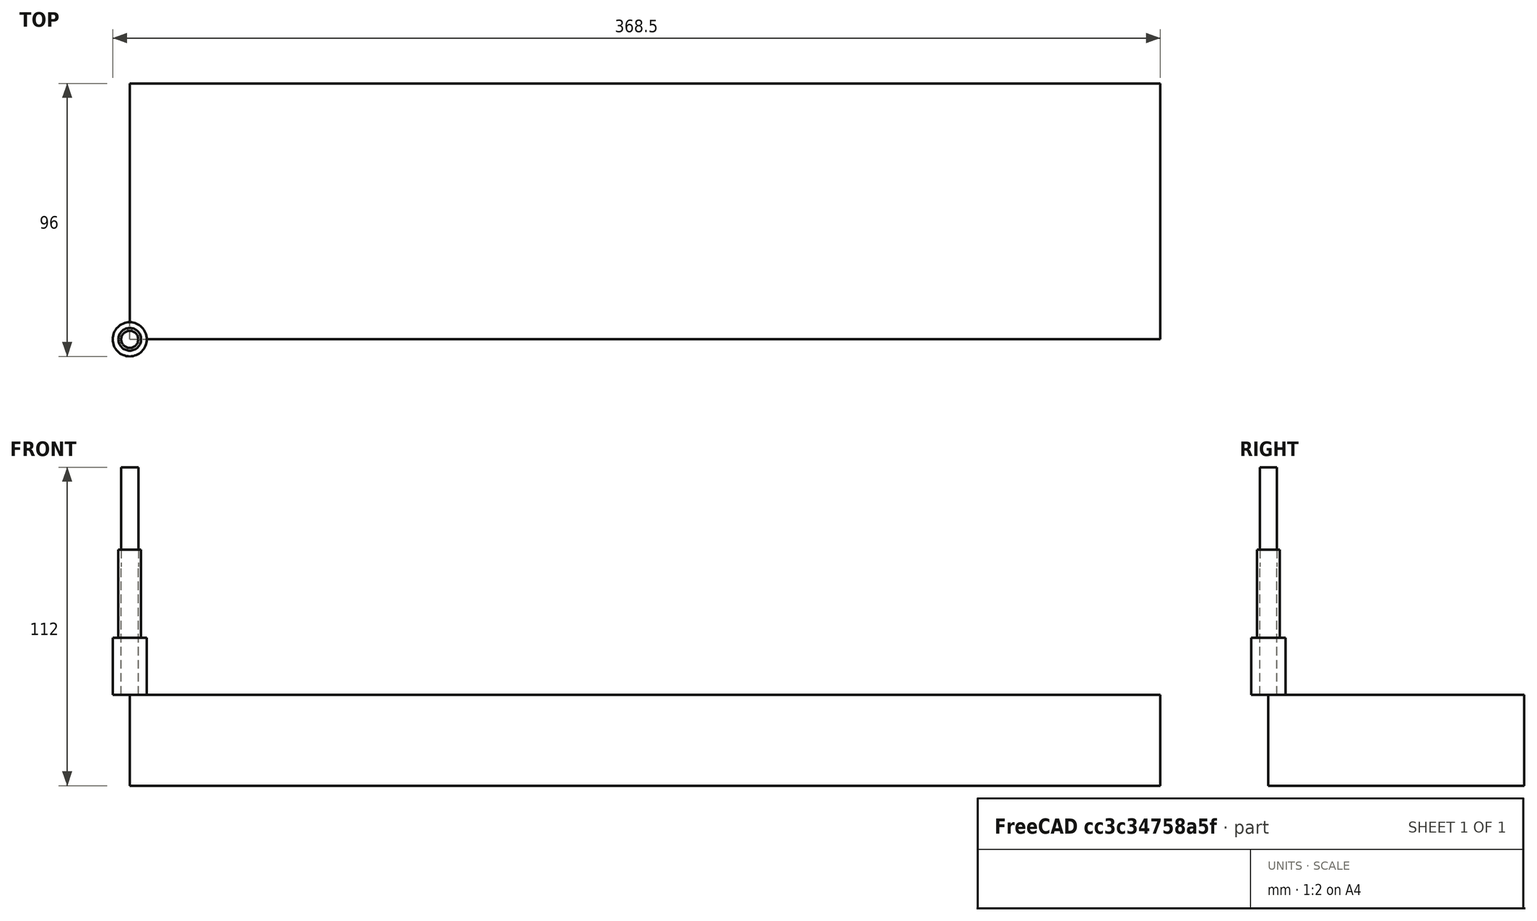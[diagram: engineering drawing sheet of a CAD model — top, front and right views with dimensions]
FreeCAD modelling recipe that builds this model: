
FCSTD DOCUMENT  (FreeCAD 0.22R34789 (Git))
Label: fence_side_reversal
License: All rights reserved
LicenseURL: http://en.wikipedia.org/wiki/All_rights_reserved
objects: Path::FeaturePython×7, Part::FeaturePython×5, App::DocumentObjectGroup×3, App::FeaturePython×1
note: 8 computed .brp shape members not serialized (recipe doc carries the construction recipe); baked Part::Feature solids carry a one-line shape summary decoded from their .brp

FEATURE [Part::FeaturePython] b_drill_press_table_001_  label="drill_press_table_fence_face_r_001"  # a2plus imported part (geometry in sourceFile) (typed FeaturePython)
  Placement = pos=(0,0,0) rot=(1,0,0;1.5708rad)
  a2p_Version = 0.4.61
  fixedPosition = true
  objectType = a2pPart
  sourceFile = ./../drill_press_table.FCStd
  sourcePart = fence_face_r
  subassemblyImport = false
  timeLastImport = 1.69948e+09
  updateColors = true
FEATURE [App::FeaturePython] SetupSheet  # Path/CAM operation (typed FeaturePython)
  ClearanceHeightExpression = OpStockZMax+SetupSheet.ClearanceHeightOffset
  ClearanceHeightOffset = 5
  CoolantMode = 0
  CoolantModes = None | Flood | Mist
  FinalDepthExpression = OpFinalDepth
  HorizRapid = 0
  SafeHeightExpression = OpStockZMax+SetupSheet.SafeHeightOffset
  SafeHeightOffset = 3
  StartDepthExpression = OpStartDepth
  StepDownExpression = OpToolDiameter
  VertRapid = 0
FEATURE [Part::FeaturePython] Clone  label="Model-drill_press_table_fence_face_r_001"  # Draft clone (typed FeaturePython)
  AttacherType = Attacher::AttachEngine3D
  Fuse = false
  Objects = -> [b_drill_press_table_001_]
  PathResource = Model
  Placement = pos=(-7.5,116,-306) rot=(1,0,0;1.5708rad)
  Scale = (1,1,1)
FEATURE [App::DocumentObjectGroup] Model
  Group = -> [Clone]
FEATURE [Part::FeaturePython] Stock  # WARN: FeaturePython — macro-defined, semantics opaque (R4)
  Base = -> Model
  ExtXneg = 15
  ExtXpos = 10
  ExtYneg = 15
  ExtYpos = 10
  ExtZneg = 0
  ExtZpos = 0
  Placement = pos=(15,15,-32) rot=(0,0,1;0rad)
  StockType = FromBase
FEATURE [Part::FeaturePython] ToolBit001  label="6 mm endmill, D=6, H=45, L=80, S=6"  # Path/CAM toolbit (typed FeaturePython)
  BitPropertyNames = Chipload | CuttingEdgeHeight | Diameter | Flutes | Length | Material | ShankDiameter | SpindleDirection
  BitShape = <userpath>/.local/share/FreeCAD/Macro/Tools/Shape/endmill.fcstd
  Chipload = 0
  CuttingEdgeHeight = 45
  Diameter = 6
  File = <userpath>/.local/share/FreeCAD/Macro/Tools/Bit/03c10998-7ce6-11ee-8713-1065300da2fe.fctb
  Flutes = 2
  Length = 80
  Material = 1
  ShankDiameter = 6
  ShapeName = endmill
  SpindleDirection = 0
FEATURE [Path::FeaturePython] TC__6_mm_endmill__D_6__H_45__L_80__S_6  label="TC: 6 mm endmill, D=6, H=45, L=80, S=6"  # Path/CAM operation (typed FeaturePython)
  HorizFeed = 10
  HorizRapid = 0
  SpindleDir = 0
  SpindleSpeed = 0
  Tool = -> ToolBit001
  ToolNumber = 17
  VertFeed = 1
  VertRapid = 0
  expr: HorizRapid = SetupSheet.HorizRapid
  expr: VertRapid = SetupSheet.VertRapid
FEATURE [Path::FeaturePython] Profile  # Path/CAM operation (typed FeaturePython)
  Active = true
  AreaParams:
    Tolerance = 1e-07
    FitArcs = True
    Simplify = False
    CleanDistance = 0.0
    Accuracy = 0.01
    Unit = 1.0
    MinArcPoints = 4
    MaxArcPoints = 100
    ClipperScale = 10000000.0
    Fill = 0
    Coplanar = 0
    Reorient = True
    Outline = False
    Explode = False
    OpenMode = 0
    Deflection = 0.01
    SubjectFill = 0
    ClipFill = 0
    Offset = -3.0
    ExtraPass = 0
    Stepover = 0.0
    LastStepover = 0.0
    JoinType = 0
    EndType = 0
    MiterLimit = 2.0
    RoundPrecision = 0.0
    PocketMode = 0
    ToolRadius = 1.0
    PocketExtraOffset = 0.0
    PocketStepover = 0.0
    PocketLastStepover = 0.0
    FromCenter = False
    Angle = 45.0
    AngleShift = 0.0
    Shift = 0.0
    Thicken = False
    SectionCount = -1
    Stepdown = 1.0
    SectionOffset = 0.0
    SectionTolerance = 1e-07
    SectionMode = 2
    Project = False
  ClearanceHeight = 5
  CoolantMode = 0
  CycleTime = 00:15:28
  Direction = 0
  FinalDepth = -22
  HandleMultipleFeatures = 0
  JoinType = 0
  MiterLimit = 0.1
  OffsetExtra = 0
  OpFinalDepth = -32
  OpStartDepth = -2.13e-14
  OpStockZMax = -2.13e-14
  OpStockZMin = -32
  OpToolDiameter = 6
  PathParams = {'orientation': 1, 'feedrate': 10.0, 'feedrate_v': 1.0, 'verbose': True, 'resume_height': 2.9999999999999787, 'retraction': 4.999999999999979, 'return_end': True, 'preamble': False}
  SafeHeight = 3
  Side = 1
  SplitArcs = false
  StartDepth = -2.13e-14
  StartPoint = (0,0,0)
  StepDown = 2
  ToolController = -> TC__6_mm_endmill__D_6__H_45__L_80__S_6
  UseComp = true
  UseStartPoint = false
  processCircles = false
  processHoles = false
  processPerimeter = true
  expr: ClearanceHeight = OpStockZMax + SetupSheet.ClearanceHeightOffset
  expr: FinalDepth = OpFinalDepth + 10 mm
  expr: SafeHeight = OpStockZMax + SetupSheet.SafeHeightOffset
  expr: StartDepth = OpStartDepth
  expr: StepDown = OpToolDiameter / 3
FEATURE [Path::FeaturePython] DressupDogbone  # Path/CAM operation (typed FeaturePython)
  Base = -> Profile
  Custom = 0
  Incision = 0
  Side = 0
  Style = 0
FEATURE [Path::FeaturePython] DressupTag  # Path/CAM operation (typed FeaturePython)
  Angle = 45
  Base = -> DressupDogbone
  Height = 8
  Positions = (4) [(100.875,77,0),(266.625,77,0),(259.1,18,0),(108.4,18,0)]
  Radius = 0
  SegmentationFactor = 50
  Width = 12
FEATURE [Part::FeaturePython] endmill_D_12__H_20__S_8  label="endmill D=12, H=20, S=8"  # Path/CAM toolbit (typed FeaturePython)
  BitPropertyNames = Chipload | CuttingEdgeHeight | Diameter | Flutes | Length | Material | ShankDiameter | SpindleDirection
  BitShape = <userpath>/.local/share/FreeCAD/Macro/Tools/Shape/endmill.fcstd
  Chipload = 0
  CuttingEdgeHeight = 20
  Diameter = 12
  File = <userpath>/.local/share/FreeCAD/Macro/Tools/Bit/d4c3dad8-7323-11ee-af98-1065300da2fe.fctb
  Flutes = 2
  Length = 51
  Material = 0
  ShankDiameter = 8
  ShapeName = endmill
  SpindleDirection = 0
FEATURE [Path::FeaturePython] TC__endmill_D_12__H_20__S_8  label="TC: endmill D=12, H=20, S=8"  # Path/CAM operation (typed FeaturePython)
  HorizFeed = 100
  HorizRapid = 0
  SpindleDir = 0
  SpindleSpeed = 0
  Tool = -> endmill_D_12__H_20__S_8
  ToolNumber = 14
  VertFeed = 1
  VertRapid = 0
  expr: HorizRapid = SetupSheet.HorizRapid
  expr: VertRapid = SetupSheet.VertRapid
FEATURE [App::DocumentObjectGroup] Tools
  Group = -> [TC__6_mm_endmill__D_6__H_45__L_80__S_6,TC__endmill_D_12__H_20__S_8]
FEATURE [Path::FeaturePython] Pocket_Shape  # Path/CAM operation (typed FeaturePython)
  Active = true
  AreaParams:
    Tolerance = 1e-07
    FitArcs = True
    Simplify = False
    CleanDistance = 0.0
    Accuracy = 0.01
    Unit = 1.0
    MinArcPoints = 4
    MaxArcPoints = 100
    ClipperScale = 10000000.0
    Fill = 0
    Coplanar = 0
    Reorient = True
    Outline = False
    Explode = False
    OpenMode = 0
    Deflection = 0.01
    SubjectFill = 0
    ClipFill = 0
    Offset = 0.0
    ExtraPass = 0
    Stepover = 0.0
    LastStepover = 0.0
    JoinType = 0
    EndType = 0
    MiterLimit = 2.0
    RoundPrecision = 0.0
    PocketMode = 2
    ToolRadius = 6.0
    PocketExtraOffset = 0.0
    PocketStepover = 6.0
    PocketLastStepover = 0.0
    FromCenter = True
    Angle = 45.0
    AngleShift = 0.0
    Shift = 0.0
    Thicken = False
    SectionCount = -1
    Stepdown = 1.0
    SectionOffset = 0.0
    SectionTolerance = 1e-07
    SectionMode = 2
    Project = False
  Base = -> [Clone]
  ClearanceHeight = 5
  CoolantMode = 0
  CutMode = 0
  CycleTime = 00:03:20
  ExtensionCorners = true
  ExtensionFeature = -> [Clone]
  ExtensionLengthDefault = 6
  ExtraOffset = 0
  FinalDepth = -6
  FinishDepth = 0
  KeepToolDown = false
  MinTravel = false
  OffsetPattern = 1
  OpFinalDepth = -6
  OpStartDepth = -1.42e-14
  OpStockZMax = -2.13e-14
  OpStockZMin = -32
  OpToolDiameter = 12
  PathParams = {'orientation': 1, 'feedrate': 100.0, 'feedrate_v': 1.0, 'verbose': True, 'resume_height': 2.9999999999999787, 'retraction': 4.999999999999979, 'return_end': True, 'preamble': False}
  PocketLastStepOver = 0
  SafeHeight = 3
  SplitArcs = false
  StartAt = 0
  StartDepth = -1.42e-14
  StartPoint = (0,0,0)
  StepDown = 2
  StepOver = 50
  ToolController = -> TC__endmill_D_12__H_20__S_8
  UseOutline = false
  UseRestMachining = false
  UseStartPoint = false
  ZigZagAngle = 45
  expr: ClearanceHeight = OpStockZMax + SetupSheet.ClearanceHeightOffset
  expr: ExtensionLengthDefault = OpToolDiameter / 2
  expr: FinalDepth = OpFinalDepth
  expr: SafeHeight = OpStockZMax + SetupSheet.SafeHeightOffset
  expr: StartDepth = OpStartDepth
  expr: StepDown = OpToolDiameter / 6
FEATURE [App::DocumentObjectGroup] Operations
  Group = -> [DressupTag,Pocket_Shape]
FEATURE [Path::FeaturePython] Job  # Path/CAM operation (typed FeaturePython)
  CycleTime = 00:18:48
  Fixtures = G54
  GeometryTolerance = 0.01
  JobType = 0
  Model = -> Model
  Operations = -> Operations
  OrderOutputBy = 0
  PostProcessor = 3
  PostProcessorOutputFile = %D/%d
  SetupSheet = -> SetupSheet
  SplitOutput = false
  Stock = -> Stock
  Tools = -> Tools
